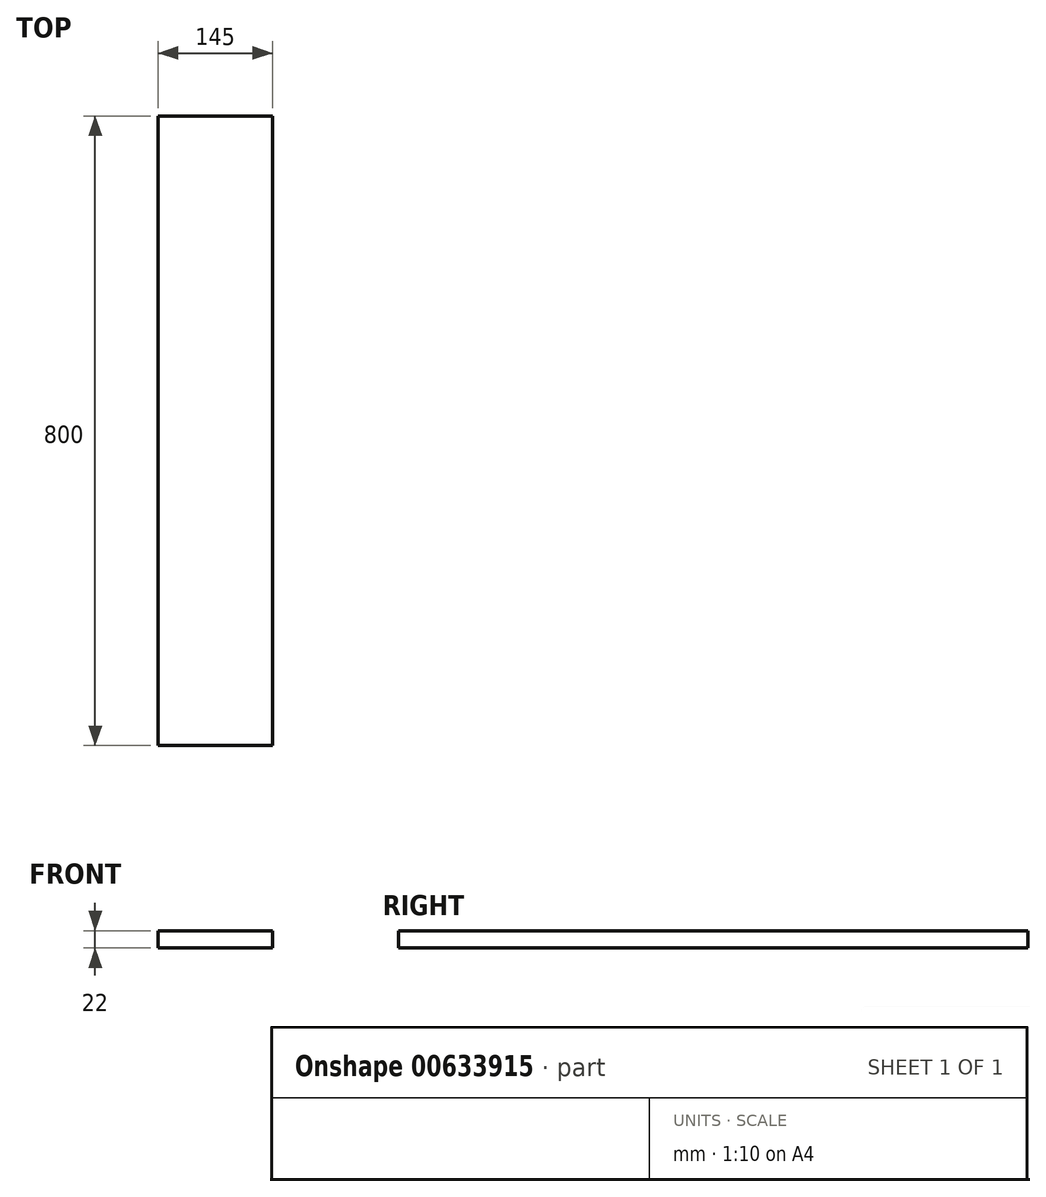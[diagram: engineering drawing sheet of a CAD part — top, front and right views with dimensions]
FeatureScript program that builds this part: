
annotation { "Feature Type Name" : "Feature", "Feature Type Description" : "" }
export const myFeature = defineFeature(function(context is Context, id is Id, definition is map)
    precondition{}
    {
        {
            var Q0;
            Q0=qCreatedBy(makeId("Top.planeOp"),FACE);
            var sketch = newSketch(context, id + "F0", { "sketchPlane" : qUnion([Q0])});
            skLineSegment(sketch, "E0.bottom", {"start": v(0, 0) * mm, "end": v(145, 0) * mm});
            skLineSegment(sketch, "E0.top", {"start": v(0, 800) * mm, "end": v(145, 800) * mm});
            skLineSegment(sketch, "E0.left", {"start": v(0, 0) * mm, "end": v(0, 800) * mm});
            skLineSegment(sketch, "E0.right", {"start": v(145, 0) * mm, "end": v(145, 800) * mm});
            skSolve(sketch);
        }
        {
            var Q0;
            Q0=makeQuery(id+"F0.imprint","IMPRINT",FACE,{"disambiguationData":[TD([[makeQuery(id+"F0.imprint","IMPRINT",EDGE,{"derivedFrom":sQuery(id+"F0.wireOp",EDGE,"E0.bottom")}),1.0]])]});
            extrude(context, id + "F1", {"entities" : qUnion([Q0]), "depth" : 22 * mm, "offsetDistance" : 25 * mm});
        }
    });
